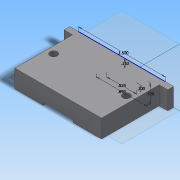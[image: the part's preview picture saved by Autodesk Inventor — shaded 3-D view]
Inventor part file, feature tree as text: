
AUTODESK INVENTOR PART (.ipt)
format: ipt  version: 2014 SP2 (Build 180246200, 246)  size: 125,952 bytes
history: native  units: in
note: dims shown in document units (in); Inventor stores cm internally (conversion verified against a paired STEP export)
features: sketch x3, extrude x3, hole x1, mirror x1, other x1
ambient origin geometry x8: Origin, YZ Plane, XZ Plane, XY Plane, X Axis, Y Axis, Z Axis, Center Point
bodies: Solid1 (feature_tree)
feature tree (9):
  sketch  "Sketch1"  dims[d0=0.89in d1=0.33in]
  extrude  "Extrusion1"  Depth=0.89in
  extrude  "Extrusion2"  Depth=1.5in
  extrude  "Extrusion3"  Depth=1.03in TaperAngle=0.0deg
  hole  "Hole1"  [1 undecoded]
  mirror  "Mirror1"
  other  "iFeature1:1"
  sketch  "Sketch3"  dims[d2=1.1in d3=0.0in d4=1.5in]
  sketch  "Sketch4"  dims[d5=0.15in d6=1.03in d7=0.0in d8=0.52in d9=0.1in d10=1.0in d11=0.0in d12=0.55in d13=0.63in d14=0.129in d15=0.75in d16=0.225in d17=0.25in d18=0.5635in d19=1.0in d20=0.8108in d21=0.15in]
note: 1 required parameter value undecoded (feature->parameter linkage not recoverable at this tier; creation-order binding heuristic only, values carry confidence <= 0.55)
